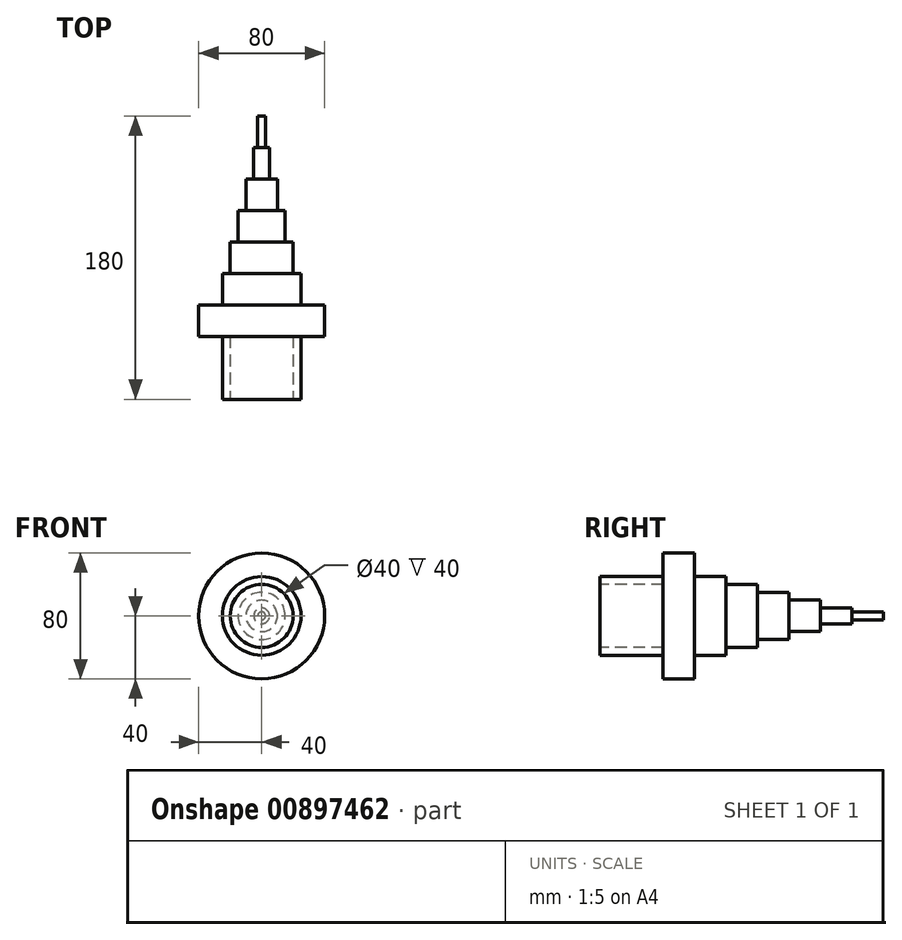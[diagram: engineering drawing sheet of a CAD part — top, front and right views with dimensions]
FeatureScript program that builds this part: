
annotation { "Feature Type Name" : "Feature", "Feature Type Description" : "" }
export const myFeature = defineFeature(function(context is Context, id is Id, definition is map)
    precondition{}
    {
        {
            var Q0;
            Q0=qCreatedBy(makeId("Front.planeOp"),FACE);
            var sketch = newSketch(context, id + "F0", { "sketchPlane" : qUnion([Q0])});
            skCircle(sketch, "E0", {"center": v(0, 0) * mm, "radius": 40 * mm});
            skSolve(sketch);
        }
        {
            var Q0;
            Q0=makeQuery(id+"F0.imprint","IMPRINT",FACE,{"disambiguationData":[TD([[makeQuery(id+"F0.imprint","IMPRINT",EDGE,{"derivedFrom":sQuery(id+"F0.wireOp",EDGE,"E0")}),1.0]])]});
            extrude(context, id + "F1", {"entities" : qUnion([Q0]), "depth" : 20 * mm, "offsetDistance" : 25.4 * mm});
        }
        {
            var Q0;
            Q0=makeQuery(id+"F1.opExtrude","CAP_FACE",FACE,{"disambiguationData":[OSD([sQuery(id+"F0.wireOp",EDGE,"E0")])],"isStart":false});
            var sketch = newSketch(context, id + "F2", { "sketchPlane" : qUnion([Q0])});
            skCircle(sketch, "E1", {"center": v(0, 0) * mm, "radius": 25 * mm});
            skSolve(sketch);
        }
        {
            var Q0;
            Q0=makeQuery(id+"F2.imprint","IMPRINT",FACE,{"disambiguationData":[TD([[makeQuery(id+"F2.imprint","IMPRINT",EDGE,{"derivedFrom":sQuery(id+"F2.wireOp",EDGE,"E1")}),1.0]])]});
            extrude(context, id + "F3", {"entities" : qUnion([Q0]), "operationType" : NewBodyOperationType.ADD, "depth" : 40 * mm, "offsetDistance" : 25.4 * mm});
        }
        {
            var Q0;
            Q0=makeQuery(id+"F3.opExtrude","CAP_FACE",FACE,{"disambiguationData":[OSD([sQuery(id+"F2.wireOp",EDGE,"E1")])],"isStart":false});
            var sketch = newSketch(context, id + "F4", { "sketchPlane" : qUnion([Q0])});
            skCircle(sketch, "E2", {"center": v(0, 0) * mm, "radius": 20 * mm});
            skSolve(sketch);
        }
        {
            var Q0;
            Q0=makeQuery(id+"F4.imprint","IMPRINT",FACE,{"disambiguationData":[TD([[makeQuery(id+"F4.imprint","IMPRINT",EDGE,{"derivedFrom":sQuery(id+"F4.wireOp",EDGE,"E2")}),1.0]])]});
            extrude(context, id + "F5", {"entities" : qUnion([Q0]), "operationType" : NewBodyOperationType.REMOVE, "oppositeDirection" : true, "depth" : 40 * mm, "offsetDistance" : 25.4 * mm});
        }
        {
            var Q0;
            Q0=makeQuery(id+"F1.opExtrude","CAP_FACE",FACE,{"disambiguationData":[OSD([sQuery(id+"F0.wireOp",EDGE,"E0")])],"isStart":true});
            var sketch = newSketch(context, id + "F6", { "sketchPlane" : qUnion([Q0])});
            skCircle(sketch, "E3", {"center": v(0, 0) * mm, "radius": 25 * mm});
            skSolve(sketch);
        }
        {
            var Q0;
            Q0=makeQuery(id+"F6.imprint","IMPRINT",FACE,{"disambiguationData":[TD([[makeQuery(id+"F6.imprint","IMPRINT",EDGE,{"derivedFrom":sQuery(id+"F6.wireOp",EDGE,"E3")}),1.0]])]});
            extrude(context, id + "F7", {"entities" : qUnion([Q0]), "operationType" : NewBodyOperationType.ADD, "depth" : 20 * mm, "offsetDistance" : 25.4 * mm});
        }
        {
            var Q0;
            Q0=makeQuery(id+"F7.opExtrude","CAP_FACE",FACE,{"disambiguationData":[OSD([sQuery(id+"F6.wireOp",EDGE,"E3")])],"isStart":false});
            var sketch = newSketch(context, id + "F8", { "sketchPlane" : qUnion([Q0])});
            skCircle(sketch, "E4", {"center": v(0, 0) * mm, "radius": 20 * mm});
            skSolve(sketch);
        }
        {
            var Q0;
            Q0=makeQuery(id+"F8.imprint","IMPRINT",FACE,{"disambiguationData":[TD([[makeQuery(id+"F8.imprint","IMPRINT",EDGE,{"derivedFrom":sQuery(id+"F8.wireOp",EDGE,"E4")}),1.0]])]});
            extrude(context, id + "F9", {"entities" : qUnion([Q0]), "operationType" : NewBodyOperationType.ADD, "depth" : 20 * mm, "offsetDistance" : 25.4 * mm});
        }
        {
            var Q0;
            Q0=makeQuery(id+"F9.opExtrude","CAP_FACE",FACE,{"disambiguationData":[OSD([sQuery(id+"F8.wireOp",EDGE,"E4")])],"isStart":false});
            var sketch = newSketch(context, id + "F10", { "sketchPlane" : qUnion([Q0])});
            skCircle(sketch, "E5", {"center": v(0, 0) * mm, "radius": 15 * mm});
            skSolve(sketch);
        }
        {
            var Q0;
            Q0=makeQuery(id+"F10.imprint","IMPRINT",FACE,{"disambiguationData":[TD([[makeQuery(id+"F10.imprint","IMPRINT",EDGE,{"derivedFrom":sQuery(id+"F10.wireOp",EDGE,"E5")}),1.0]])]});
            extrude(context, id + "F11", {"entities" : qUnion([Q0]), "operationType" : NewBodyOperationType.ADD, "depth" : 20 * mm, "offsetDistance" : 25.4 * mm});
        }
        {
            var Q0;
            Q0=makeQuery(id+"F11.opExtrude","CAP_FACE",FACE,{"disambiguationData":[OSD([sQuery(id+"F10.wireOp",EDGE,"E5")])],"isStart":false});
            var sketch = newSketch(context, id + "F12", { "sketchPlane" : qUnion([Q0])});
            skCircle(sketch, "E6", {"center": v(0, 0) * mm, "radius": 10 * mm});
            skSolve(sketch);
        }
        {
            var Q0;
            Q0 = qSketchRegion(id + "F12", true);
            extrude(context, id + "F13", {"entities" : qUnion([Q0]), "operationType" : NewBodyOperationType.ADD, "depth" : 20 * mm, "offsetDistance" : 25.4 * mm});
        }
        {
            var Q0;
            Q0=makeQuery(id+"F13.opExtrude","CAP_FACE",FACE,{"disambiguationData":[OSD([sQuery(id+"F12.wireOp",EDGE,"E6")])],"isStart":false});
            var sketch = newSketch(context, id + "F14", { "sketchPlane" : qUnion([Q0])});
            skCircle(sketch, "E7", {"center": v(0, 0) * mm, "radius": 5 * mm});
            skSolve(sketch);
        }
        {
            var Q0;
            Q0=makeQuery(id+"F14.imprint","IMPRINT",FACE,{"disambiguationData":[TD([[makeQuery(id+"F14.imprint","IMPRINT",EDGE,{"derivedFrom":sQuery(id+"F14.wireOp",EDGE,"E7")}),1.0]])]});
            extrude(context, id + "F15", {"entities" : qUnion([Q0]), "operationType" : NewBodyOperationType.ADD, "depth" : 20 * mm, "offsetDistance" : 25.4 * mm});
        }
        {
            var Q0;
            Q0=makeQuery(id+"F15.opExtrude","CAP_FACE",FACE,{"disambiguationData":[OSD([sQuery(id+"F14.wireOp",EDGE,"E7")])],"isStart":false});
            var sketch = newSketch(context, id + "F16", { "sketchPlane" : qUnion([Q0])});
            skCircle(sketch, "E8", {"center": v(0, 0) * mm, "radius": 2.5 * mm});
            skSolve(sketch);
        }
        {
            var Q0;
            Q0 = qSketchRegion(id + "F16", true);
            extrude(context, id + "F17", {"entities" : qUnion([Q0]), "operationType" : NewBodyOperationType.ADD, "depth" : 20 * mm, "offsetDistance" : 25.4 * mm});
        }
    });
